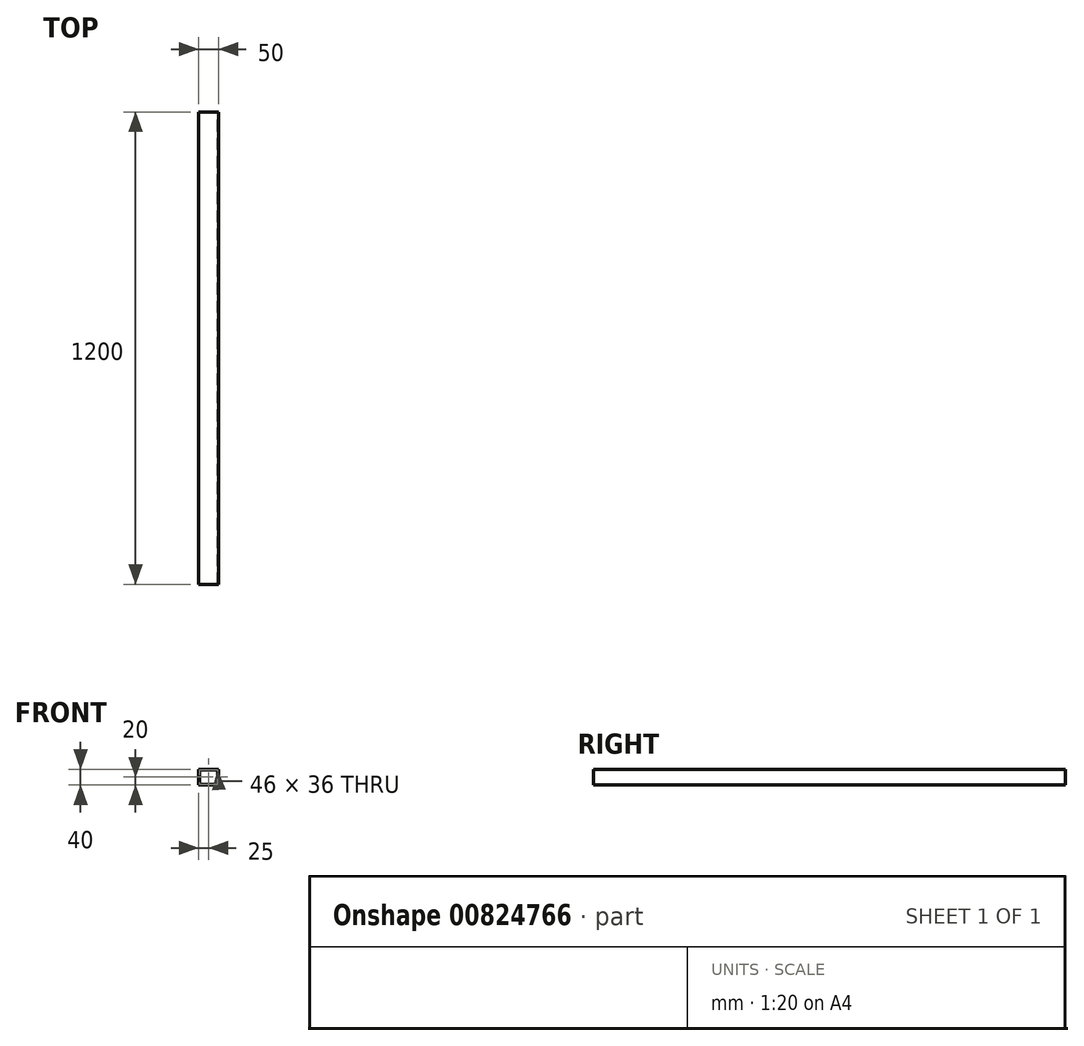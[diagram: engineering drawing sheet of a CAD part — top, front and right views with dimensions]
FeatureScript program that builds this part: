
annotation { "Feature Type Name" : "Feature", "Feature Type Description" : "" }
export const myFeature = defineFeature(function(context is Context, id is Id, definition is map)
    precondition{}
    {
        {
            var Q0;
            Q0=qCreatedBy(makeId("Front.planeOp"),FACE);
            var sketch = newSketch(context, id + "F0", { "sketchPlane" : qUnion([Q0])});
            skLineSegment(sketch, "E0.bottom", {"start": v(25, 20) * mm, "end": v(-25, 20) * mm});
            skLineSegment(sketch, "E0.top", {"start": v(25, -20) * mm, "end": v(-25, -20) * mm});
            skLineSegment(sketch, "E0.left", {"start": v(25, 20) * mm, "end": v(25, -20) * mm});
            skLineSegment(sketch, "E0.right", {"start": v(-25, 20) * mm, "end": v(-25, -20) * mm});
            skPoint(sketch, "E0.middle", {"position": v(0, 0) * mm});
            skLineSegment(sketch, "E1.bottom", {"start": v(23, 18) * mm, "end": v(-23, 18) * mm});
            skLineSegment(sketch, "E1.top", {"start": v(23, -18) * mm, "end": v(-23, -18) * mm});
            skLineSegment(sketch, "E1.left", {"start": v(23, 18) * mm, "end": v(23, -18) * mm});
            skLineSegment(sketch, "E1.right", {"start": v(-23, 18) * mm, "end": v(-23, -18) * mm});
            skSolve(sketch);
        }
        {
            var Q0;
            Q0=makeQuery(id+"F0.imprint","IMPRINT",FACE,{"disambiguationData":[TD([[makeQuery(id+"F0.imprint","IMPRINT",EDGE,{"derivedFrom":sQuery(id+"F0.wireOp",EDGE,"E0.bottom")}),1.0]])]});
            extrude(context, id + "F1", {"entities" : qUnion([Q0]), "depth" : 1200 * mm, "offsetDistance" : 25 * mm});
        }
        {
            var Q0;
            Q0=makeQuery(id+"F1.opExtrude","SWEPT_FACE",FACE,{"disambiguationData":[OSD([sQuery(id+"F0.wireOp",EDGE,"E0.top")])]});
            var sketch = newSketch(context, id + "F2", { "sketchPlane" : qUnion([Q0])});
            skLineSegment(sketch, "E2", {"start": v(25, 1200) * mm, "end": v(10, 1200) * mm});
            skLineSegment(sketch, "E3", {"start": v(10, 1200) * mm, "end": v(10, 1180) * mm});
            skCircle(sketch, "E4", {"center": v(10, 1180) * mm, "radius": 3 * mm});
            skSolve(sketch);
        }
        {
            var Q0;
            Q0=makeQuery(id+"F1.opExtrude","SWEPT_FACE",FACE,{"disambiguationData":[OSD([sQuery(id+"F0.wireOp",EDGE,"E0.bottom")])]});
            var sketch = newSketch(context, id + "F3", { "sketchPlane" : qUnion([Q0])});
            skLineSegment(sketch, "E5", {"start": v(25, -600) * mm, "end": v(0, -600) * mm});
            skSolve(sketch);
        }
    });
